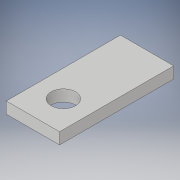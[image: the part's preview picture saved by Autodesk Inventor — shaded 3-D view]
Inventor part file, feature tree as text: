
AUTODESK INVENTOR PART (.ipt)
format: ipt  version: 2019.4 (Build 234330000, 330)  size: 98,304 bytes
history: native  units: in
note: dims shown in document units (in); Inventor stores cm internally (conversion verified against a paired STEP export)
features: extrude x1, sketch x1
ambient origin geometry x8: Origin, YZ Plane, XZ Plane, XY Plane, X Axis, Y Axis, Z Axis, Center Point
bodies: Solid1 (feature_tree)
feature tree (2):
  extrude  "Extrusion1"  Depth=0.2756in
  sketch  "Sketch1"  dims[d0=0.5906in d1=0.2756in d2=0.126in d3=0.1575in d4=0.0591in d5=0.0in]
